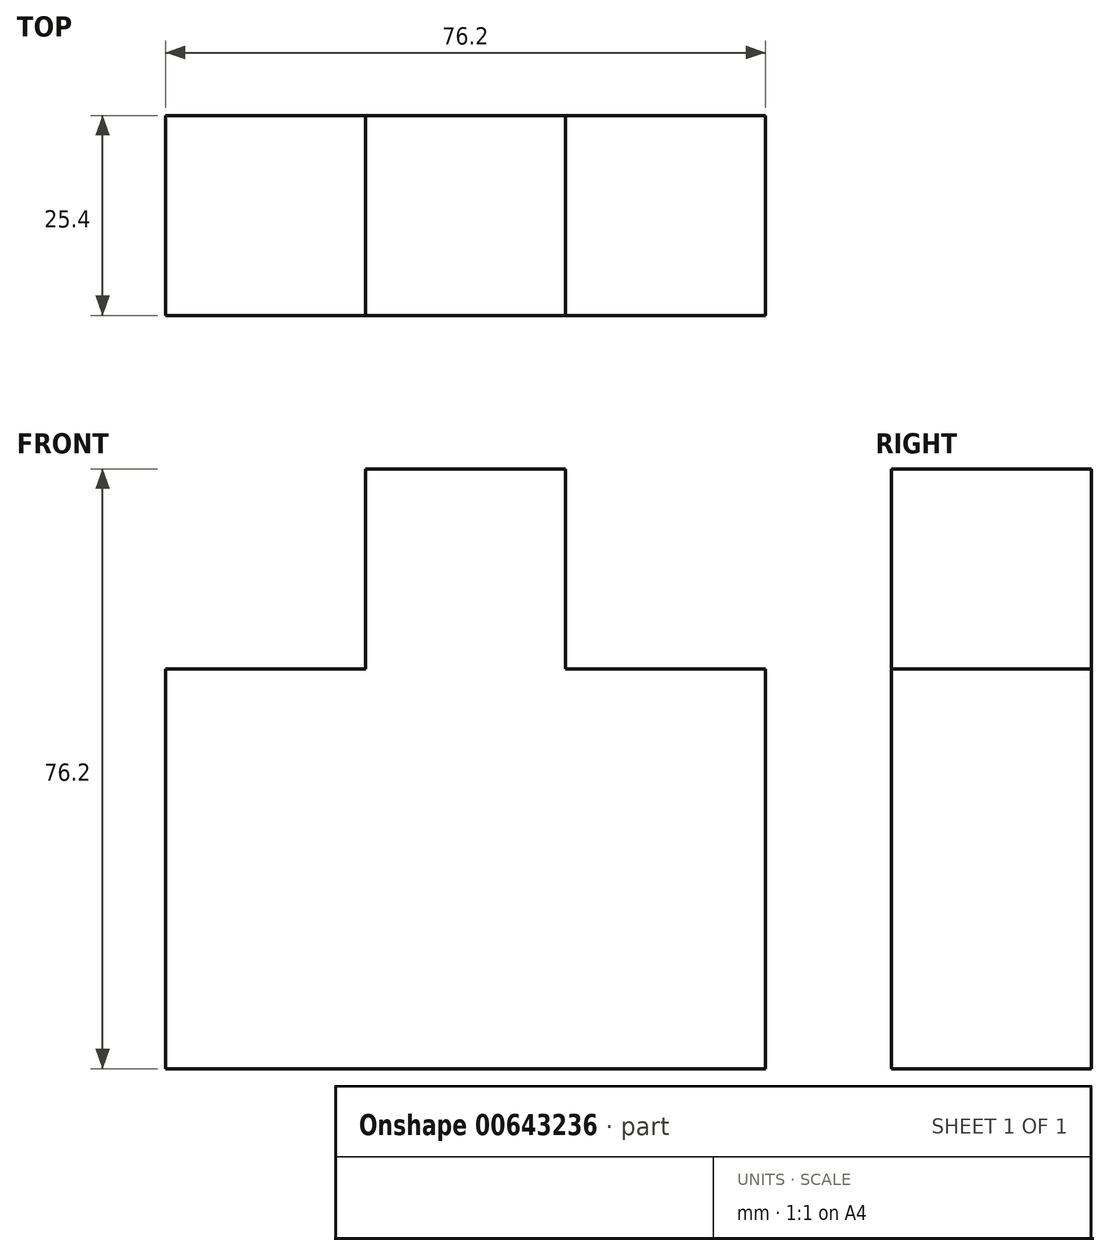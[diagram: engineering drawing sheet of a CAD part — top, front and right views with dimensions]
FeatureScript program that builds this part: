
annotation { "Feature Type Name" : "Feature", "Feature Type Description" : "" }
export const myFeature = defineFeature(function(context is Context, id is Id, definition is map)
    precondition{}
    {
        {
            var Q0;
            Q0=qCreatedBy(makeId("Front.planeOp"),FACE);
            var sketch = newSketch(context, id + "F0", { "sketchPlane" : qUnion([Q0])});
            skLineSegment(sketch, "E0.bottom", {"start": v(-33.43, 0) * mm, "end": v(-8.03, 0) * mm});
            skLineSegment(sketch, "E0.top", {"start": v(-33.43, 25.4) * mm, "end": v(-8.03, 25.4) * mm});
            skLineSegment(sketch, "E0.left", {"start": v(-33.43, 0) * mm, "end": v(-33.43, 25.4) * mm});
            skLineSegment(sketch, "E0.right", {"start": v(-8.03, 0) * mm, "end": v(-8.03, 25.4) * mm});
            skLineSegment(sketch, "E1.bottom", {"start": v(-8.03, 25.4) * mm, "end": v(17.37, 25.4) * mm});
            skLineSegment(sketch, "E1.top", {"start": v(-8.03, 0) * mm, "end": v(17.37, 0) * mm});
            skLineSegment(sketch, "E1.left", {"start": v(-8.03, 25.4) * mm, "end": v(-8.03, 0) * mm});
            skLineSegment(sketch, "E1.right", {"start": v(17.37, 25.4) * mm, "end": v(17.37, 0) * mm});
            skLineSegment(sketch, "E2.bottom", {"start": v(17.37, 25.4) * mm, "end": v(42.77, 25.4) * mm});
            skLineSegment(sketch, "E2.top", {"start": v(17.37, 0) * mm, "end": v(42.77, 0) * mm});
            skLineSegment(sketch, "E2.right", {"start": v(42.77, 25.4) * mm, "end": v(42.77, 0) * mm});
            skLineSegment(sketch, "E3.top", {"start": v(-33.43, 50.8) * mm, "end": v(-8.03, 50.8) * mm});
            skLineSegment(sketch, "E3.left", {"start": v(-33.43, 25.4) * mm, "end": v(-33.43, 50.8) * mm});
            skLineSegment(sketch, "E3.right", {"start": v(-8.03, 25.4) * mm, "end": v(-8.03, 50.8) * mm});
            skLineSegment(sketch, "E4.bottom", {"start": v(-8.03, 50.8) * mm, "end": v(17.37, 50.8) * mm});
            skLineSegment(sketch, "E4.left", {"start": v(-8.03, 50.8) * mm, "end": v(-8.03, 25.4) * mm});
            skLineSegment(sketch, "E4.right", {"start": v(17.37, 50.8) * mm, "end": v(17.37, 25.4) * mm});
            skLineSegment(sketch, "E5.bottom", {"start": v(17.37, 50.8) * mm, "end": v(42.77, 50.8) * mm});
            skLineSegment(sketch, "E5.right", {"start": v(42.77, 50.8) * mm, "end": v(42.77, 25.4) * mm});
            skLineSegment(sketch, "E6.top", {"start": v(-8.03, 76.2) * mm, "end": v(17.37, 76.2) * mm});
            skLineSegment(sketch, "E6.left", {"start": v(-8.03, 50.8) * mm, "end": v(-8.03, 76.2) * mm});
            skLineSegment(sketch, "E6.right", {"start": v(17.37, 50.8) * mm, "end": v(17.37, 76.2) * mm});
            skSolve(sketch);
        }
        {
            var Q0;
            Q0=makeQuery(id+"F0.imprint","IMPRINT",FACE,{"disambiguationData":[TD([[makeQuery(id+"F0.imprint","IMPRINT",EDGE,{"derivedFrom":sQuery(id+"F0.wireOp",EDGE,"E4.bottom")}),1.0]])]});
            var Q1;
            Q1=makeQuery(id+"F0.imprint","IMPRINT",FACE,{"disambiguationData":[TD([[makeQuery(id+"F0.imprint","IMPRINT",EDGE,{"derivedFrom":sQuery(id+"F0.wireOp",EDGE,"E0.top")}),1.0]])]});
            var Q2;
            Q2=makeQuery(id+"F0.imprint","IMPRINT",FACE,{"disambiguationData":[TD([[makeQuery(id+"F0.imprint","IMPRINT",EDGE,{"derivedFrom":sQuery(id+"F0.wireOp",EDGE,"E1.bottom")}),1.0]])]});
            var Q3;
            Q3=makeQuery(id+"F0.imprint","IMPRINT",FACE,{"disambiguationData":[TD([[makeQuery(id+"F0.imprint","IMPRINT",EDGE,{"derivedFrom":sQuery(id+"F0.wireOp",EDGE,"E5.bottom")}),-1.0]])]});
            var Q4;
            Q4=makeQuery(id+"F0.imprint","IMPRINT",FACE,{"disambiguationData":[TD([[makeQuery(id+"F0.imprint","IMPRINT",EDGE,{"derivedFrom":sQuery(id+"F0.wireOp",EDGE,"E0.bottom")}),1.0]])]});
            var Q5;
            Q5=makeQuery(id+"F0.imprint","IMPRINT",FACE,{"disambiguationData":[TD([[makeQuery(id+"F0.imprint","IMPRINT",EDGE,{"derivedFrom":sQuery(id+"F0.wireOp",EDGE,"E1.top")}),1.0]])]});
            var Q6;
            Q6=makeQuery(id+"F0.imprint","IMPRINT",FACE,{"disambiguationData":[TD([[makeQuery(id+"F0.imprint","IMPRINT",EDGE,{"derivedFrom":sQuery(id+"F0.wireOp",EDGE,"E2.top")}),1.0]])]});
            extrude(context, id + "F1", {"entities" : qUnion([Q0, Q1, Q2, Q3, Q4, Q5, Q6]), "depth" : 25.4 * mm, "offsetDistance" : 25.4 * mm});
        }
    });
